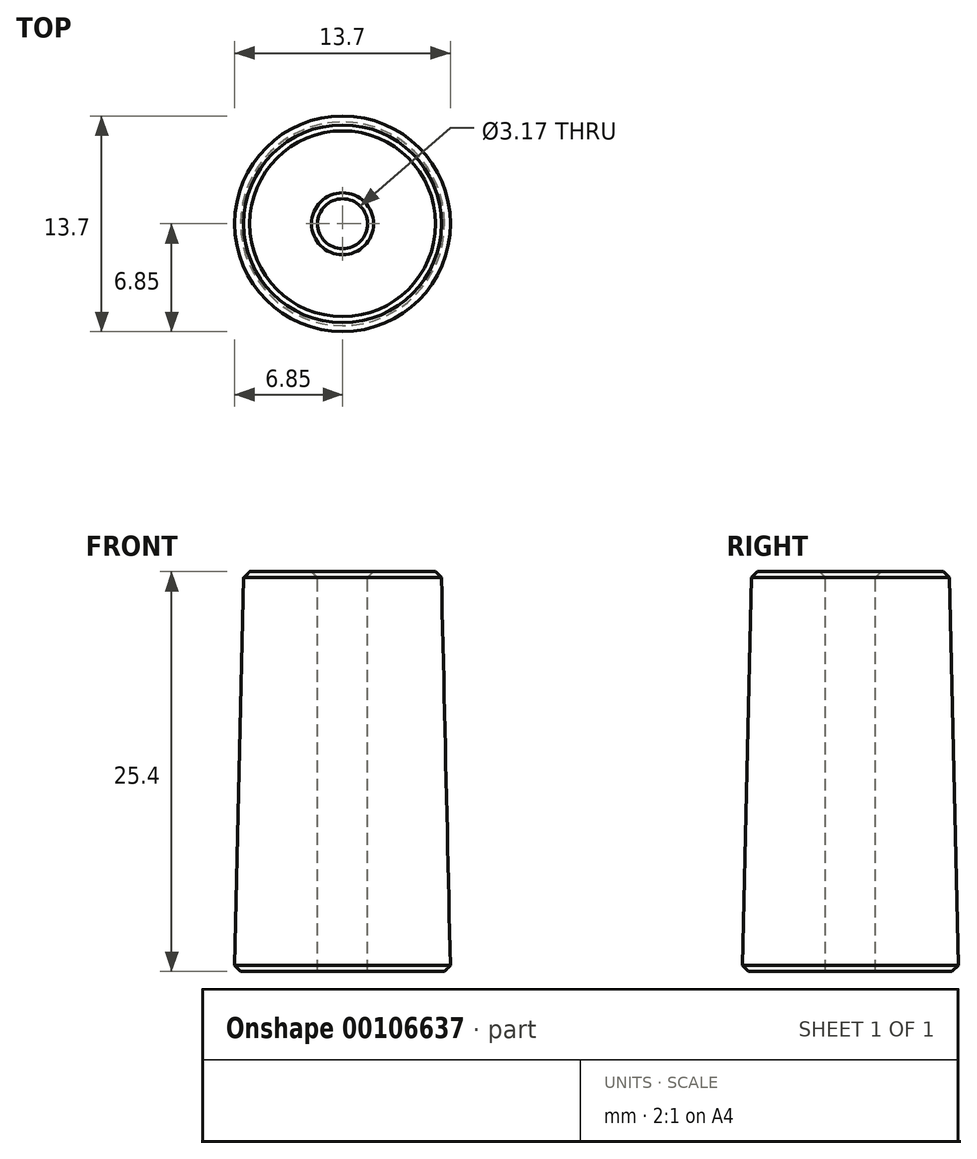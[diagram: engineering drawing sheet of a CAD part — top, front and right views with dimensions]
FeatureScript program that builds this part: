
annotation { "Feature Type Name" : "Feature", "Feature Type Description" : "" }
export const myFeature = defineFeature(function(context is Context, id is Id, definition is map)
    precondition{}
    {
        {
            var Q0;
            Q0=qCreatedBy(makeId("Front.planeOp"),FACE);
            var sketch = newSketch(context, id + "F0", { "sketchPlane" : qUnion([Q0])});
            skLineSegment(sketch, "E0", {"start": v(0, 0) * mm, "end": v(6.86, 0) * mm});
            skLineSegment(sketch, "E1", {"start": v(6.86, 0) * mm, "end": v(6.27, 25.4) * mm});
            skLineSegment(sketch, "E2", {"start": v(6.27, 25.4) * mm, "end": v(1.59, 25.4) * mm});
            skLineSegment(sketch, "E3", {"start": v(0, 25.4) * mm, "end": v(0, 0) * mm});
            skLineSegment(sketch, "E4", {"start": v(1.59, 0) * mm, "end": v(1.59, 25.4) * mm});
            skSolve(sketch);
        }
        {
            var Q0;
            Q0 = qSketchRegion(id + "F0", true);
            var Q1;
            Q1=sQuery(id+"F0.wireOp",EDGE,"E3");
            revolve(context, id + "F1", {"entities" : qUnion([Q0]), "axis" : qUnion([Q1]), "revolveType" : RevolveType.FULL});
        }
        {
            var Q0;
            Q0=makeQuery(id+"F1.opRevolve","SWEPT_EDGE",EDGE,{"disambiguationData":[OSD([sQuery(id+"F0.wireOp",EDGE,"E1"),sQuery(id+"F0.wireOp",EDGE,"E2")])]});
            var Q1;
            Q1=makeQuery(id+"F1.opRevolve","SWEPT_EDGE",EDGE,{"disambiguationData":[OSD([sQuery(id+"F0.wireOp",EDGE,"E2"),sQuery(id+"F0.wireOp",EDGE,"E4")])]});
            var Q2;
            Q2=makeQuery(id+"F1.opRevolve","SWEPT_EDGE",EDGE,{"disambiguationData":[OSD([sQuery(id+"F0.wireOp",EDGE,"E0"),sQuery(id+"F0.wireOp",EDGE,"E1")])]});
            chamfer(context, id + "F2", {"entities" : qUnion([Q0, Q1, Q2]), "width" : 0.38 * mm, "tangentPropagation" : true});
        }
    });
